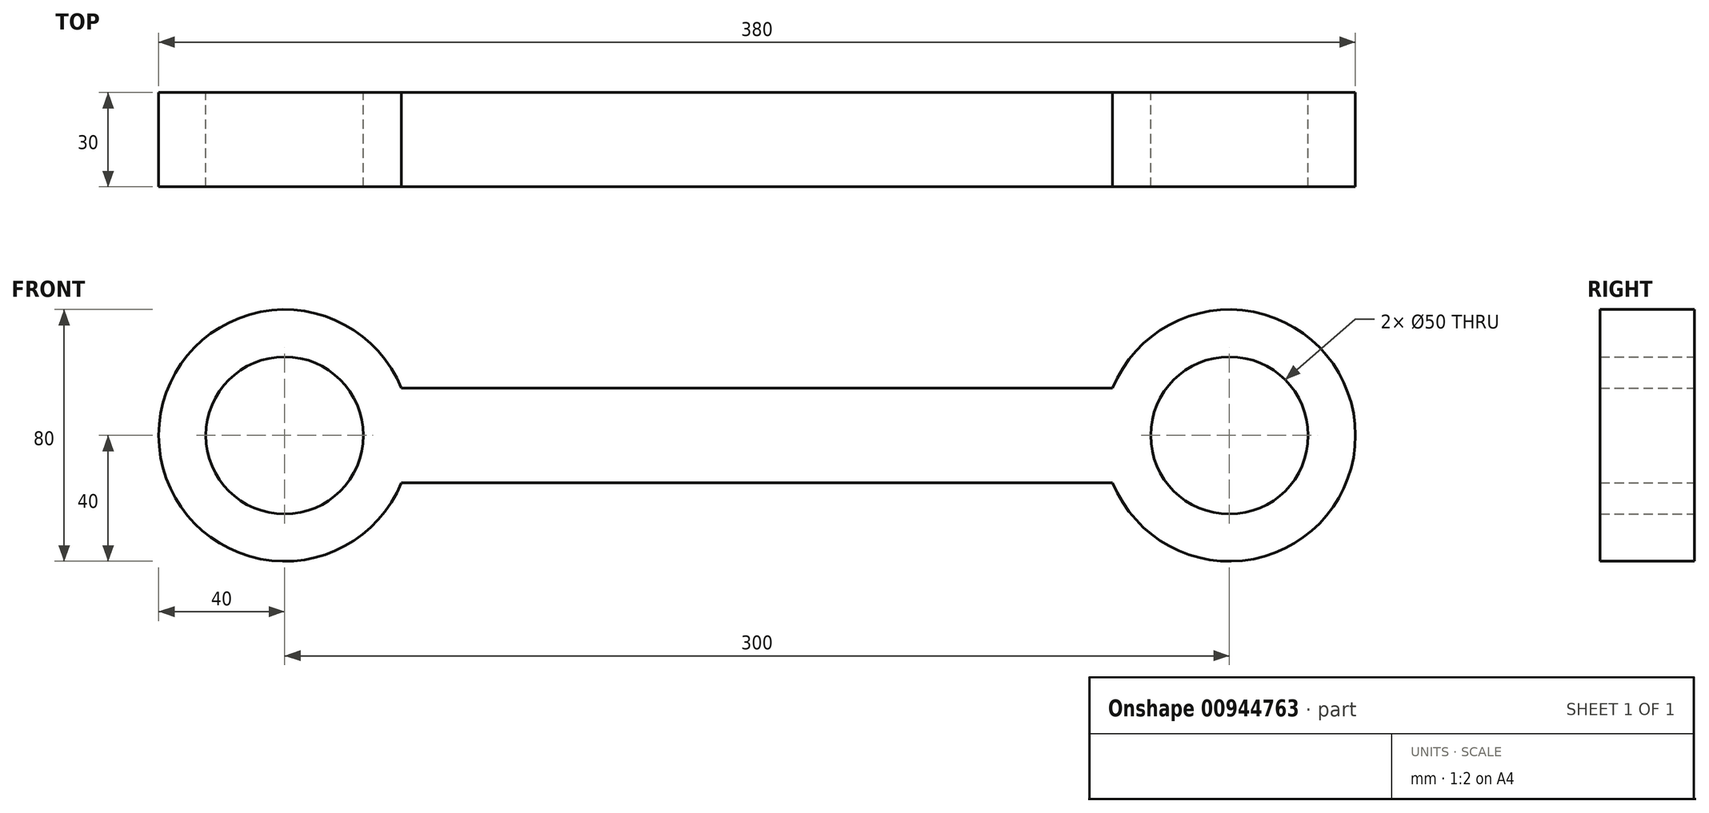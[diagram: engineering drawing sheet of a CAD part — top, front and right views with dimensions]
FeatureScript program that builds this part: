
annotation { "Feature Type Name" : "Feature", "Feature Type Description" : "" }
export const myFeature = defineFeature(function(context is Context, id is Id, definition is map)
    precondition{}
    {
        {
            var Q0;
            Q0=qCreatedBy(makeId("Front.planeOp"),FACE);
            var sketch = newSketch(context, id + "F0", { "sketchPlane" : qUnion([Q0])});
            skCircle(sketch, "E0", {"center": v(-150, 0) * mm, "radius": 25 * mm});
            skCircle(sketch, "E1", {"center": v(150, 0) * mm, "radius": 25 * mm});
            skArc(sketch, "E2", {"start": v(-112.92, 15) * mm, "mid": v(-190, 0) * mm, "end": v(-112.92, -15) * mm});
            skArc(sketch, "E3", {"start": v(112.92, -15) * mm, "mid": v(190, 0) * mm, "end": v(112.92, 15) * mm});
            skLineSegment(sketch, "E4.bottom", {"start": v(112.92, -15) * mm, "end": v(-112.92, -15) * mm});
            skLineSegment(sketch, "E4.top", {"start": v(112.92, 15) * mm, "end": v(-112.92, 15) * mm});
            skLineSegment(sketch, "E4.left", {"start": v(112.92, -15) * mm, "end": v(112.92, 15) * mm, "construction": true});
            skLineSegment(sketch, "E4.right", {"start": v(-112.92, -15) * mm, "end": v(-112.92, 15) * mm, "construction": true});
            skPoint(sketch, "E4.middle", {"position": v(0, 0) * mm});
            skLineSegment(sketch, "E5", {"start": v(-250.43, 0) * mm, "end": v(205.1, 0) * mm, "construction": true});
            skSolve(sketch);
        }
        {
            var Q0;
            Q0 = qSketchRegion(id + "F0", true);
            extrude(context, id + "F1", {"entities" : qUnion([Q0]), "endBound" : BoundingType.SYMMETRIC, "depth" : 30 * mm, "offsetDistance" : 25 * mm});
        }
    });
